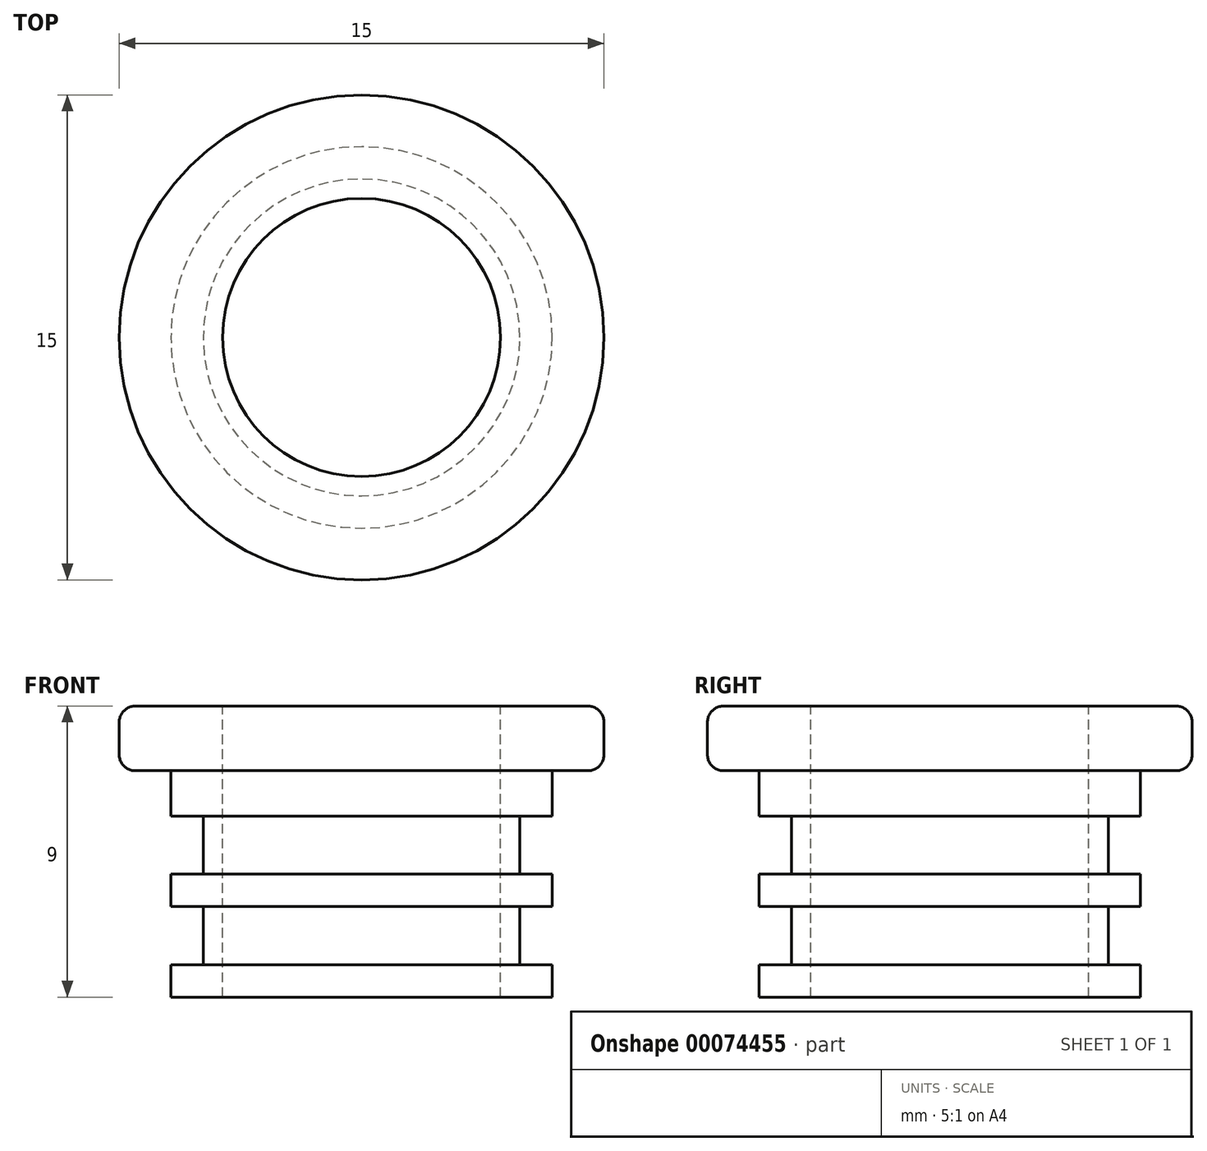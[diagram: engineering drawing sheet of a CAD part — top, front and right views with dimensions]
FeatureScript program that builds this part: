
annotation { "Feature Type Name" : "Feature", "Feature Type Description" : "" }
export const myFeature = defineFeature(function(context is Context, id is Id, definition is map)
    precondition{}
    {
        {
            var Q0;
            Q0=qCreatedBy(makeId("Front.planeOp"),FACE);
            var sketch = newSketch(context, id + "F0", { "sketchPlane" : qUnion([Q0])});
            skLineSegment(sketch, "E0", {"start": v(0, 11.44) * mm, "end": v(0, -10.47) * mm, "construction": true});
            skLineSegment(sketch, "E1", {"start": v(-4.3, 9) * mm, "end": v(-7.5, 9) * mm});
            skLineSegment(sketch, "E2", {"start": v(-7.5, 9) * mm, "end": v(-7.5, 7) * mm});
            skLineSegment(sketch, "E3", {"start": v(-7.5, 7) * mm, "end": v(-5.9, 7) * mm});
            skLineSegment(sketch, "E4", {"start": v(-5.9, 7) * mm, "end": v(-5.9, 5.6) * mm});
            skLineSegment(sketch, "E5", {"start": v(-5.9, 5.6) * mm, "end": v(-4.9, 5.6) * mm});
            skLineSegment(sketch, "E6", {"start": v(-4.9, 5.6) * mm, "end": v(-4.9, 3.8) * mm});
            skLineSegment(sketch, "E7", {"start": v(-4.9, 3.8) * mm, "end": v(-5.9, 3.8) * mm});
            skLineSegment(sketch, "E8", {"start": v(-5.9, 3.8) * mm, "end": v(-5.9, 2.8) * mm});
            skLineSegment(sketch, "E9", {"start": v(-5.9, 2.8) * mm, "end": v(-4.9, 2.8) * mm});
            skLineSegment(sketch, "E10", {"start": v(-4.9, 2.8) * mm, "end": v(-4.9, 1) * mm});
            skLineSegment(sketch, "E11", {"start": v(-4.9, 1) * mm, "end": v(-5.9, 1) * mm});
            skLineSegment(sketch, "E12", {"start": v(-5.9, 1) * mm, "end": v(-5.9, 0) * mm});
            skLineSegment(sketch, "E13", {"start": v(-5.9, 0) * mm, "end": v(-4.3, 0) * mm});
            skLineSegment(sketch, "E14", {"start": v(-4.3, 9) * mm, "end": v(-4.3, 0) * mm});
            skSolve(sketch);
        }
        {
            var Q0;
            Q0 = qSketchRegion(id + "F0", true);
            var Q1;
            Q1=sQuery(id+"F0.wireOp",EDGE,"E0");
            revolve(context, id + "F1", {"entities" : qUnion([Q0]), "axis" : qUnion([Q1]), "revolveType" : RevolveType.FULL});
        }
        {
            var Q0;
            Q0=makeQuery(id+"F1.opRevolve","SWEPT_EDGE",EDGE,{"disambiguationData":[OSD([sQuery(id+"F0.wireOp",EDGE,"E1"),sQuery(id+"F0.wireOp",EDGE,"E2")])]});
            var Q1;
            Q1=makeQuery(id+"F1.opRevolve","SWEPT_EDGE",EDGE,{"disambiguationData":[OSD([sQuery(id+"F0.wireOp",EDGE,"E2"),sQuery(id+"F0.wireOp",EDGE,"E3")])]});
            fillet(context, id + "F2", {"entities" : qUnion([Q0, Q1]), "radius" : .5 * mm, "tangentPropagation" : true, "allowEdgeOverflow" : false});
        }
    });
